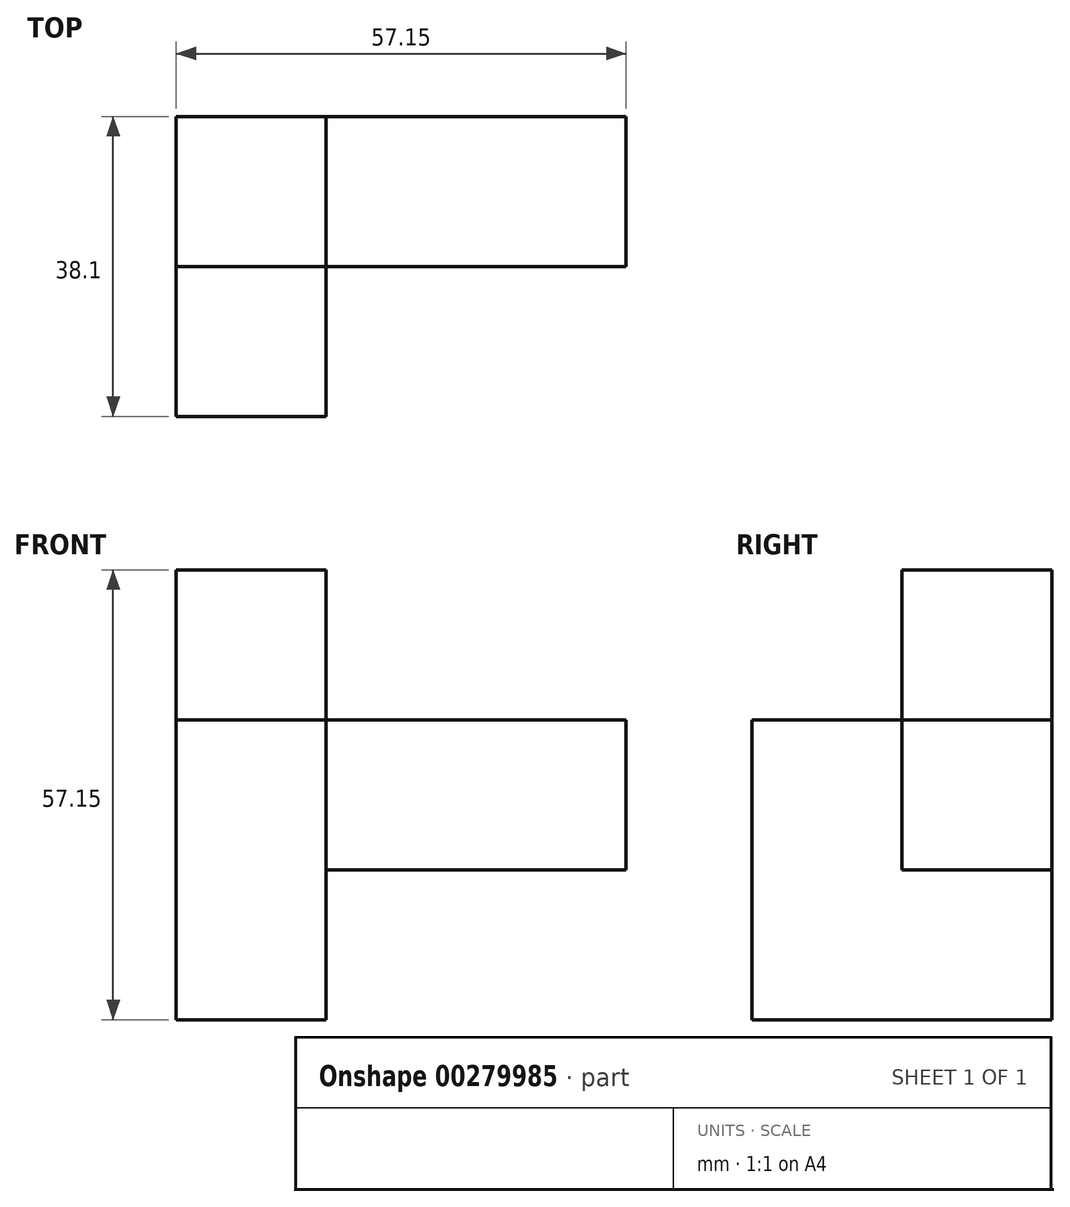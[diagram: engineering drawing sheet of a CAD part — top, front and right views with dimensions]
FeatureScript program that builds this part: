
annotation { "Feature Type Name" : "Feature", "Feature Type Description" : "" }
export const myFeature = defineFeature(function(context is Context, id is Id, definition is map)
    precondition{}
    {
        {
            var Q0;
            Q0=qCreatedBy(makeId("Top.planeOp"),FACE);
            var sketch = newSketch(context, id + "F0", { "sketchPlane" : qUnion([Q0])});
            skLineSegment(sketch, "E0.bottom", {"start": v(0, 0) * mm, "end": v(19.05, 0) * mm});
            skLineSegment(sketch, "E0.top", {"start": v(0, 38.1) * mm, "end": v(19.05, 38.1) * mm});
            skLineSegment(sketch, "E0.left", {"start": v(0, 0) * mm, "end": v(0, 38.1) * mm});
            skLineSegment(sketch, "E0.right", {"start": v(19.05, 0) * mm, "end": v(19.05, 38.1) * mm});
            skSolve(sketch);
        }
        {
            var Q0;
            Q0 = qSketchRegion(id + "F0", true);
            extrude(context, id + "F1", {"entities" : qUnion([Q0]), "depth" : 38.1 * mm});
        }
        {
            var Q0;
            Q0=makeQuery(id+"F1.opExtrude","CAP_FACE",FACE,{"disambiguationData":[OSD([sQuery(id+"F0.wireOp",EDGE,"E0.bottom"),sQuery(id+"F0.wireOp",EDGE,"E0.top"),sQuery(id+"F0.wireOp",EDGE,"E0.left"),sQuery(id+"F0.wireOp",EDGE,"E0.right")])],"isStart":false});
            var sketch = newSketch(context, id + "F2", { "sketchPlane" : qUnion([Q0])});
            skLineSegment(sketch, "E1.bottom", {"start": v(19.05, 38.1) * mm, "end": v(0, 38.1) * mm});
            skLineSegment(sketch, "E1.top", {"start": v(19.05, 19.05) * mm, "end": v(0, 19.05) * mm});
            skLineSegment(sketch, "E1.left", {"start": v(19.05, 38.1) * mm, "end": v(19.05, 19.05) * mm});
            skLineSegment(sketch, "E1.right", {"start": v(0, 38.1) * mm, "end": v(0, 19.05) * mm});
            skSolve(sketch);
        }
        {
            var Q0;
            Q0 = qSketchRegion(id + "F2", true);
            extrude(context, id + "F3", {"entities" : qUnion([Q0]), "operationType" : NewBodyOperationType.ADD, "depth" : 19.05 * mm});
        }
        {
            var Q0;
            Q0=makeQuery(id+"F3.boolean.opBoolean","MERGE",FACE,{"derivedFrom":[makeQuery(id+"F1.opExtrude","SWEPT_FACE",FACE,{"disambiguationData":[OSD([sQuery(id+"F0.wireOp",EDGE,"E0.right")])]}),makeQuery(id+"F3.opExtrude","SWEPT_FACE",FACE,{"disambiguationData":[OSD([sQuery(id+"F2.wireOp",EDGE,"E1.left")])]})]});
            var sketch = newSketch(context, id + "F4", { "sketchPlane" : qUnion([Q0])});
            skLineSegment(sketch, "E2.bottom", {"start": v(19.05, 38.1) * mm, "end": v(38.1, 38.1) * mm});
            skLineSegment(sketch, "E2.top", {"start": v(19.05, 19.05) * mm, "end": v(38.1, 19.05) * mm});
            skLineSegment(sketch, "E2.left", {"start": v(19.05, 38.1) * mm, "end": v(19.05, 19.05) * mm});
            skLineSegment(sketch, "E2.right", {"start": v(38.1, 38.1) * mm, "end": v(38.1, 19.05) * mm});
            skSolve(sketch);
        }
        {
            var Q0;
            Q0 = qSketchRegion(id + "F4", true);
            extrude(context, id + "F5", {"entities" : qUnion([Q0]), "operationType" : NewBodyOperationType.ADD, "depth" : 38.1 * mm});
        }
    });
